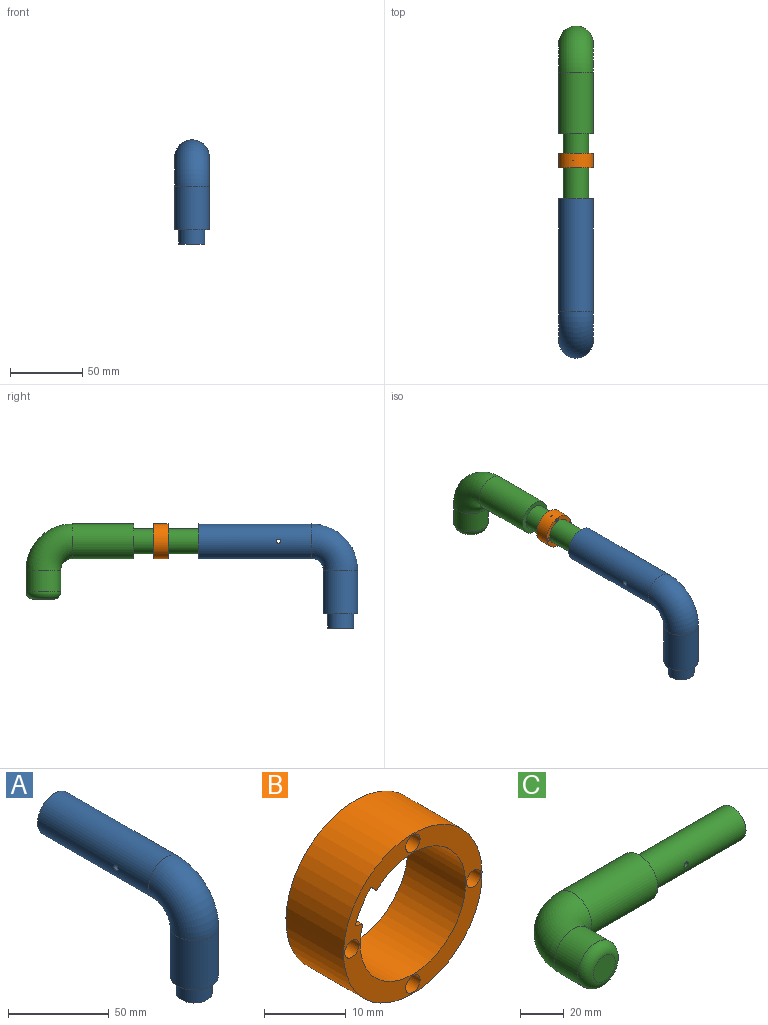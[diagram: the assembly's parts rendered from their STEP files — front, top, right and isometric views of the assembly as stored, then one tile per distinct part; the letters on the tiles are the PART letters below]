
ASSEMBLY  parts=3 mates=2
PART A: 28 faces, bbox 24x112.6x74.6 mm
  f0: cylinder r=12mm len=78mm, axis (0,1,0), area 5866.9mm2, adj f2,f11,f24,f25
  f1: plane 18x18mm, normal (0,0,-1), area 190.5mm2, adj f5,f6,f7,f8,f9
  f2: torus R=20mm, axis (1,0,0), area 2368.7mm2, adj f0,f3
  f3: cylinder r=12mm len=30mm, axis (0,0,1), area 2261.9mm2, adj f2,f4
  f4: plane 24x24mm, normal (0,0,-1), area 197.9mm2, adj f3,f5
  f5: cylinder r=9mm len=18mm, axis (0,0,1), area 565.5mm2, adj f1,f4
  f6: plane 40x8mm, normal (0,1,0), area 320mm2, adj f1,f7,f9,f10
  f7: plane 40x8mm, normal (1,0,0), area 320mm2, adj f1,f6,f8,f10
  f8: plane 40x8mm, normal (0,-1,0), area 320mm2, adj f1,f7,f9,f10
  f9: plane 40x8mm, normal (-1,0,0), area 320mm2, adj f1,f6,f8,f10
  f10: plane 8x8mm, normal (0,0,-1), area 51.4mm2, adj f6,f7,f8,f9,f26
  f11: plane 24x24mm, normal (0,1,0), area 183mm2, adj f0,f18,f19,f20,f21
  f12: plane 18.25x18.25mm, normal (0,1,0), area 211.3mm2, adj f21,f22
  f13: plane 5.31x2.72mm, normal (0,1,0), area 7.8mm2, adj f14,f18,f19,f21
  f14: plane 5x1.3mm, normal (0.5,0,0.87), area 7.5mm2, adj f13,f15,f18,f21
  f15: plane 2.84x2.36mm, normal (0,-1,0), area 3.8mm2, adj f14,f16,f18,f21
  f16: plane 35x1.48mm, normal (0.18,0,0.98), area 52.7mm2, adj f15,f17,f18,f21
  f17: plane 2.84x2.36mm, normal (0,1,0), area 3.8mm2, adj f16,f18,f20,f21
  f18: cylinder r=10.62mm len=45mm, axis (0,-1,0), area 153mm2, adj f11,f13,f14,f15,f16,f17,f19,f20
  f19: plane 45x1.5mm, normal (0,0,-1), area 67.5mm2, adj f11,f13,f18,f21
  f20: plane 5x1.3mm, normal (0.5,0,0.87), area 7.5mm2, adj f11,f17,f18,f21
  f21: cylinder r=9.12mm len=50mm, axis (0,1,0), area 2731.1mm2, adj f11,f12,f13,f14,f15,f16,f17,f19
  f22: cylinder r=4mm len=10mm, axis (0,1,0), area 236.9mm2, adj f12,f23,f24,f25
  f23: plane 8x8mm, normal (0,1,0), area 37.7mm2, adj f22,f27
  f24: cylinder r=1.5mm len=8.29mm, axis (1,0,0), area 76.3mm2, adj f0,f22
  f25: cylinder r=1.5mm len=8.29mm, axis (1,0,0), area 76.3mm2, adj f0,f22
  f26: torus R=20mm, axis (-1,0,0), area 394.8mm2, adj f10,f27
  f27: cylinder r=2mm len=18mm, axis (0,1,0), area 226.2mm2, adj f23,f26
PART B: 20 faces, bbox 24x10x24 mm
  f0: plane 24x24mm, normal (0,1,0), area 177.1mm2, adj f2,f3,f4,f7,f10,f13,f16,f17
  f1: plane 24x24mm, normal (0,-1,0), area 164.5mm2, adj f2,f3,f6,f9,f12,f15,f16,f17
  f2: cylinder r=12mm len=24mm, axis (0,-1,0), area 754mm2, adj f0,f1
  f3: cylinder r=9.12mm len=18.25mm, axis (0,-1,0), area 527.5mm2, adj f0,f1,f16,f17
  f4: cylinder r=0.75mm len=5mm, axis (0,-1,0), area 23.6mm2, adj f0,f5
  f5: plane 2.5x2.5mm, normal (0,-1,0), area 3.1mm2, adj f4,f6
  f6: cylinder r=1.25mm len=5mm, axis (0,-1,0), area 39.3mm2, adj f1,f5
  f7: cylinder r=0.75mm len=5mm, axis (0,-1,0), area 23.6mm2, adj f0,f8
  f8: plane 2.5x2.5mm, normal (0,-1,0), area 3.1mm2, adj f7,f9
  f9: cylinder r=1.25mm len=5mm, axis (0,-1,0), area 39.3mm2, adj f1,f8
  f10: cylinder r=0.75mm len=5mm, axis (0,-1,0), area 23.6mm2, adj f0,f11
  f11: plane 2.5x2.5mm, normal (0,-1,0), area 3.1mm2, adj f10,f12
  f12: cylinder r=1.25mm len=5mm, axis (0,-1,0), area 39.3mm2, adj f1,f11
  f13: cylinder r=0.75mm len=5mm, axis (0,-1,0), area 23.6mm2, adj f0,f14
  f14: plane 2.5x2.5mm, normal (0,-1,0), area 3.1mm2, adj f13,f15
  f15: cylinder r=1.25mm len=5mm, axis (0,-1,0), area 39.3mm2, adj f1,f14
  f16: plane 10x0.99mm, normal (-0.74,0,-0.68), area 13.5mm2, adj f0,f1,f3,f18
  f17: plane 10x1.29mm, normal (0.3,0,0.95), area 13.5mm2, adj f0,f1,f3,f19
  f18: cylinder r=10.57mm len=10mm, axis (0,-1,0), area 2.7mm2, adj f0,f1,f16,f19
  f19: cylinder r=10.47mm len=10mm, axis (0,-1,0), area 50.1mm2, adj f0,f1,f17,f18
PART C: 17 faces, bbox 137.1x54.6x26 mm
  f0: cylinder r=8.75mm len=60mm, axis (-1,0,0), area 3274.9mm2, adj f3,f8,f9,f10,f12,f13,f15,f16
  f1: cylinder r=4mm len=40mm, axis (1,0,0), area 990.9mm2, adj f8,f14,f15,f16
  f2: plane 14x14mm, normal (0,-1,0), area 153.9mm2, adj f7
  f3: plane 24x24mm, normal (1,0,0), area 211.9mm2, adj f0,f6
  f4: cylinder r=12mm len=24mm, axis (0,1,0), area 1131mm2, adj f5,f7
  f5: torus R=20mm, axis (0,0,-1), area 2368.7mm2, adj f4,f6
  f6: cylinder r=12mm len=42.5mm, axis (1,0,0), area 3204.4mm2, adj f3,f5
  f7: torus R=7mm, axis (0,-1,0), area 502.5mm2, adj f2,f4
  f8: plane 17.5x17.5mm, normal (1,0,0), area 190.3mm2, adj f0,f1
  f9: plane 2.43x1.56mm, normal (-1,0,0), area 3mm2, adj f0,f11,f12,f13
  f10: plane 2.43x1.56mm, normal (1,0,0), area 3mm2, adj f0,f11,f12,f13
  f11: cylinder r=10.05mm len=4.5mm, axis (1,0,0), area 11.1mm2, adj f9,f10,f12,f13
  f12: plane 4.5x1.26mm, normal (0,-0.97,0.24), area 5.8mm2, adj f0,f9,f10,f11
  f13: plane 4.5x1.3mm, normal (0,1,0), area 5.9mm2, adj f0,f9,f10,f11
  f14: plane 8x8mm, normal (1,0,0), area 50.3mm2, adj f1
  f15: cylinder r=1.5mm len=5.04mm, axis (0,-1,0), area 45.5mm2, adj f0,f1
  f16: cylinder r=1.5mm len=5.04mm, axis (0,-1,0), area 45.5mm2, adj f0,f1
PLACE A t=(-2.6,-31.49,-38.59)mm fixed
PLACE B rot(axis=(0,1,0),170deg) t=(-2.6,-10.09,-38.59)mm
PLACE C rot(axis=(0.58,-0.58,-0.58),120deg) t=(-2.6,76.11,-78.59)mm
MATE cylindrical A.f0 <-> B.f2  axis (0,1,0) through (-2.6,-70.49,-38.59)mm
MATE slider A.f18 <-> C.f0  axis (0,1,0) through (-2.6,-81.49,-38.59)mm
